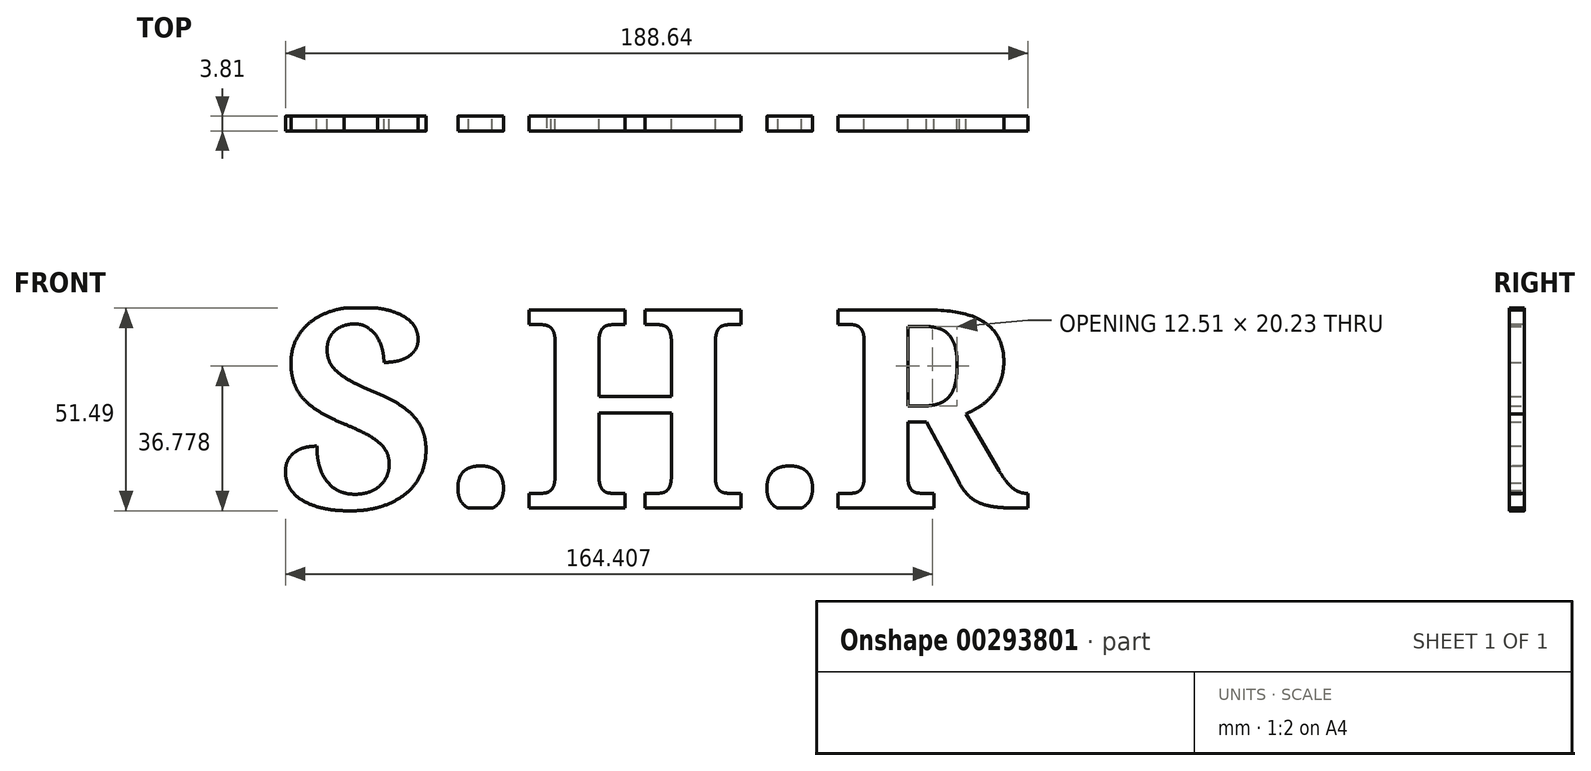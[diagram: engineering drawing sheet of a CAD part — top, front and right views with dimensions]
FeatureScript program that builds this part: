
annotation { "Feature Type Name" : "Feature", "Feature Type Description" : "" }
export const myFeature = defineFeature(function(context is Context, id is Id, definition is map)
    precondition{}
    {
        {
            var Q0;
            Q0=qCreatedBy(makeId("Front.planeOp"),FACE);
            var sketch = newSketch(context, id + "F0", { "sketchPlane" : qUnion([Q0])});
            skLineSegment(sketch, "E0.bottom", {"start": v(-97.66, 25.4) * mm, "end": v(97.66, 25.4) * mm});
            skLineSegment(sketch, "E0.top", {"start": v(-97.66, -25.4) * mm, "end": v(97.66, -25.4) * mm});
            skLineSegment(sketch, "E0.left", {"start": v(-97.66, 25.4) * mm, "end": v(-97.66, -25.4) * mm});
            skLineSegment(sketch, "E0.right", {"start": v(97.66, 25.4) * mm, "end": v(97.66, -25.4) * mm});
            skPoint(sketch, "E0.middle", {"position": v(0, 0) * mm});
            skText(sketch, "E1", { "text": "S.H.R", "fontName": "NotoSerif-Bold.ttf"});
            const initialGuessF0  = {"E1": [-0.09766, -0.0254, 1, 0, 0.0508]};
            skSetInitialGuess(sketch, initialGuessF0);
            skSolve(sketch);
        }
        {
            var Q0;
            {var subQ8=sQuery(id+"F0.wireOp",EDGE,"E1.sketch_text.stroke-0");Q0=makeQuery(id+"F0.imprint","IMPRINT",FACE,{"disambiguationData":[TD([[makeQuery(id+"F0.imprint","IMPRINT",EDGE,{"derivedFrom":subQ8}),-1.0]])]});}
            var Q1;
            Q1=makeQuery(id+"F0.imprint","IMPRINT",FACE,{"disambiguationData":[TD([[makeQuery(id+"F0.imprint","IMPRINT",EDGE,{"derivedFrom":sQuery(id+"F0.wireOp",EDGE,"E1.sketch_text.stroke-24")}),-1.0]])]});
            var Q2;
            Q2=makeQuery(id+"F0.imprint","IMPRINT",FACE,{"disambiguationData":[TD([[makeQuery(id+"F0.imprint","IMPRINT",EDGE,{"derivedFrom":sQuery(id+"F0.wireOp",EDGE,"E1.sketch_text.stroke-36")}),-1.0]])]});
            var Q3;
            Q3=makeQuery(id+"F0.imprint","IMPRINT",FACE,{"disambiguationData":[TD([[makeQuery(id+"F0.imprint","IMPRINT",EDGE,{"derivedFrom":sQuery(id+"F0.wireOp",EDGE,"E1.sketch_text.stroke-56")}),-1.0]])]});
            var Q4;
            Q4=makeQuery(id+"F0.imprint","IMPRINT",FACE,{"disambiguationData":[TD([[makeQuery(id+"F0.imprint","IMPRINT",EDGE,{"derivedFrom":sQuery(id+"F0.wireOp",EDGE,"E1.sketch_text.stroke-116")}),-1.0]])]});
            var Q5;
            Q5=makeQuery(id+"F0.imprint","IMPRINT",FACE,{"disambiguationData":[TD([[makeQuery(id+"F0.imprint","IMPRINT",EDGE,{"derivedFrom":sQuery(id+"F0.wireOp",EDGE,"E1.sketch_text.stroke-148")}),-1.0]])]});
            var Q6;
            Q6=makeQuery(id+"F0.imprint","IMPRINT",FACE,{"disambiguationData":[TD([[makeQuery(id+"F0.imprint","IMPRINT",EDGE,{"derivedFrom":sQuery(id+"F0.wireOp",EDGE,"E1.sketch_text.stroke-132")}),-1.0]])]});
            extrude(context, id + "F1", {"entities" : qUnion([Q0, Q1, Q2, Q3, Q4, Q5, Q6]), "depth" : 3.8 * mm});
        }
    });
